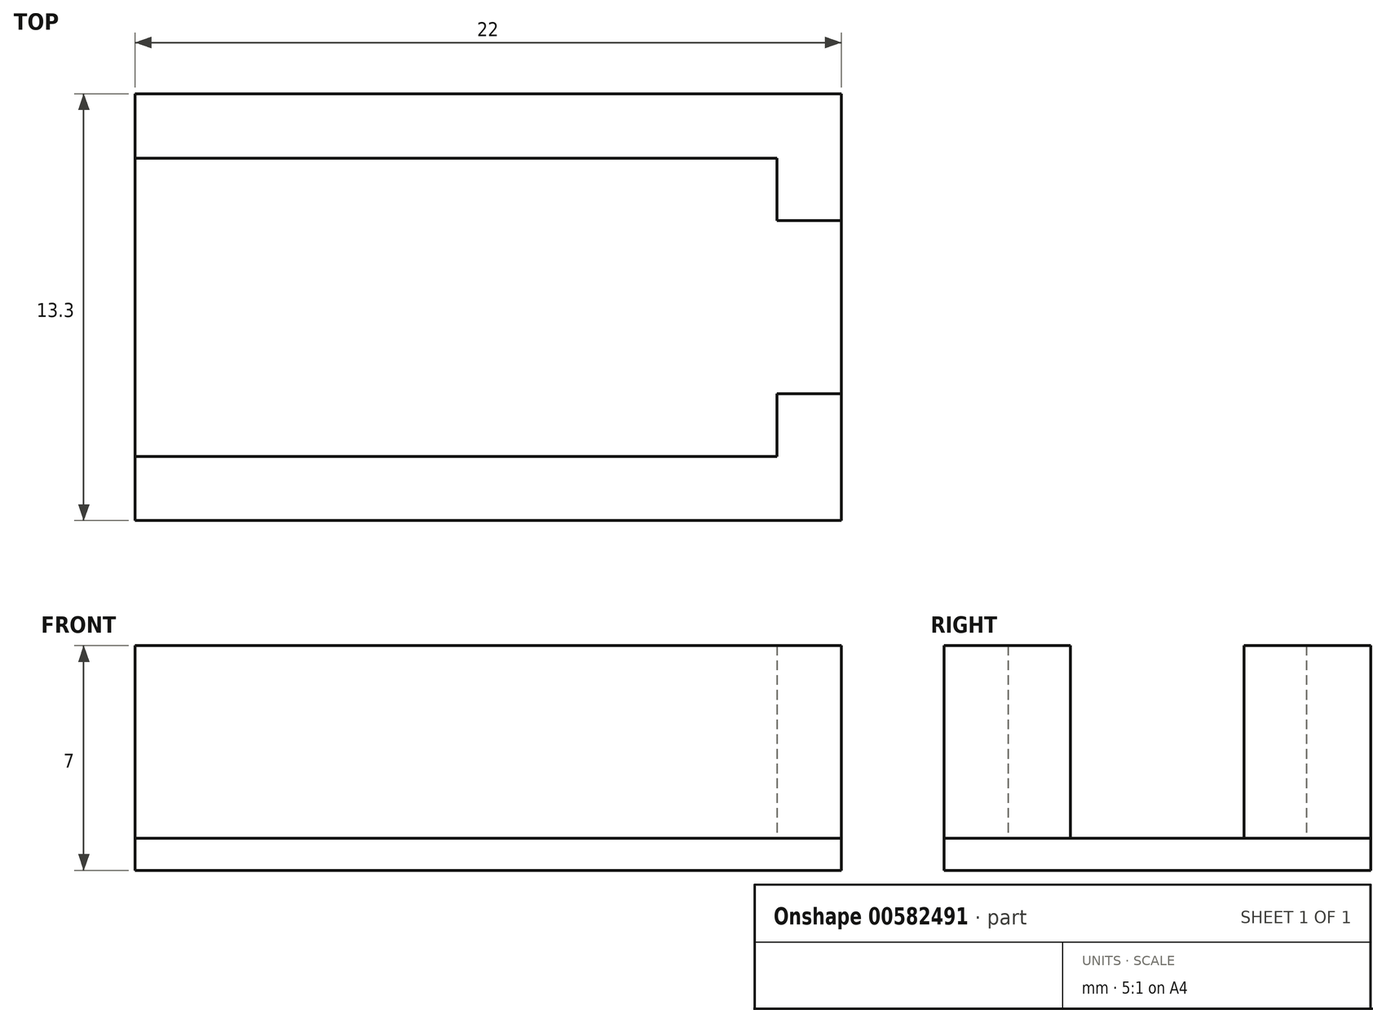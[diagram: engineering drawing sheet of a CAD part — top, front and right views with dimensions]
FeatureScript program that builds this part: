
annotation { "Feature Type Name" : "Feature", "Feature Type Description" : "" }
export const myFeature = defineFeature(function(context is Context, id is Id, definition is map)
    precondition{}
    {
        {
            var Q0;
            Q0=qCreatedBy(makeId("Top.planeOp"),FACE);
            var sketch = newSketch(context, id + "F0", { "sketchPlane" : qUnion([Q0])});
            skLineSegment(sketch, "E0.bottom", {"start": v(5, 4.65) * mm, "end": v(-5, 4.65) * mm});
            skLineSegment(sketch, "E0.top", {"start": v(5, -4.65) * mm, "end": v(-5, -4.65) * mm});
            skLineSegment(sketch, "E0.left", {"start": v(5, 4.65) * mm, "end": v(5, -4.65) * mm});
            skLineSegment(sketch, "E0.right", {"start": v(-5, 4.65) * mm, "end": v(-5, -4.65) * mm});
            skPoint(sketch, "E0.middle", {"position": v(0, 0) * mm});
            skLineSegment(sketch, "E1.0", {"start": v(5, 6.65) * mm, "end": v(-5, 6.65) * mm});
            skLineSegment(sketch, "E2.0", {"start": v(7, 4.85) * mm, "end": v(7, -4.85) * mm});
            skLineSegment(sketch, "E3.0", {"start": v(5, -6.65) * mm, "end": v(-5, -6.65) * mm});
            skLineSegment(sketch, "E4", {"start": v(5, -6.65) * mm, "end": v(7, -6.65) * mm});
            skLineSegment(sketch, "E5", {"start": v(7, -6.65) * mm, "end": v(7, -4.85) * mm});
            skLineSegment(sketch, "E6", {"start": v(7, 4.85) * mm, "end": v(7, 6.65) * mm});
            skLineSegment(sketch, "E7", {"start": v(7, 6.65) * mm, "end": v(5, 6.65) * mm});
            skLineSegment(sketch, "E8", {"start": v(-5, 6.65) * mm, "end": v(-5, 4.65) * mm});
            skLineSegment(sketch, "E9", {"start": v(-5, -6.65) * mm, "end": v(-5, -4.65) * mm});
            skLineSegment(sketch, "E10", {"start": v(5, 0) * mm, "end": v(7, 0) * mm});
            skLineSegment(sketch, "E11.bottom", {"start": v(7, 2.7) * mm, "end": v(5, 2.7) * mm});
            skLineSegment(sketch, "E11.top", {"start": v(7, -2.7) * mm, "end": v(5, -2.7) * mm});
            skLineSegment(sketch, "E11.left", {"start": v(7, 2.7) * mm, "end": v(7, -2.7) * mm});
            skLineSegment(sketch, "E11.right", {"start": v(5, 2.7) * mm, "end": v(5, -2.7) * mm});
            skPoint(sketch, "E11.middle", {"position": v(6, 0) * mm});
            skLineSegment(sketch, "E12.bottom", {"start": v(-5, 4.65) * mm, "end": v(-15, 4.65) * mm});
            skLineSegment(sketch, "E12.top", {"start": v(-5, 6.65) * mm, "end": v(-15, 6.65) * mm});
            skLineSegment(sketch, "E12.left", {"start": v(-5, 4.65) * mm, "end": v(-5, 6.65) * mm});
            skLineSegment(sketch, "E12.right", {"start": v(-15, 4.65) * mm, "end": v(-15, 6.65) * mm});
            skLineSegment(sketch, "E13.bottom", {"start": v(-5, -6.65) * mm, "end": v(-15, -6.65) * mm});
            skLineSegment(sketch, "E13.top", {"start": v(-5, -4.65) * mm, "end": v(-15, -4.65) * mm});
            skLineSegment(sketch, "E13.right", {"start": v(-15, -6.65) * mm, "end": v(-15, -4.65) * mm});
            skSolve(sketch);
        }
        {
            var Q0;
            {var subQ4=sQuery(id+"F0.wireOp",EDGE,"E0.bottom");Q0=makeQuery(id+"F0.imprint","IMPRINT",FACE,{"disambiguationData":[TD([[makeQuery(id+"F0.imprint","IMPRINT",EDGE,{"derivedFrom":subQ4}),-1.0]])]});}
            var Q1;
            {var subQ4=sQuery(id+"F0.wireOp",EDGE,"E0.top");Q1=makeQuery(id+"F0.imprint","IMPRINT",FACE,{"disambiguationData":[TD([[makeQuery(id+"F0.imprint","IMPRINT",EDGE,{"derivedFrom":subQ4}),1.0]])]});}
            var Q2;
            Q2=makeQuery(id+"F0.imprint","IMPRINT",FACE,{"disambiguationData":[TD([[makeQuery(id+"F0.imprint","IMPRINT",EDGE,{"derivedFrom":sQuery(id+"F0.wireOp",EDGE,"E13.bottom")}),-1.0]])]});
            var Q3;
            Q3=makeQuery(id+"F0.imprint","IMPRINT",FACE,{"disambiguationData":[TD([[makeQuery(id+"F0.imprint","IMPRINT",EDGE,{"derivedFrom":sQuery(id+"F0.wireOp",EDGE,"E12.bottom")}),-1.0]])]});
            extrude(context, id + "F1", {"entities" : qUnion([Q0, Q1, Q2, Q3]), "depth" : 6 * mm, "offsetDistance" : 25 * mm});
        }
        {
            var Q0;
            Q0=qCreatedBy(makeId("Top.planeOp"),FACE);
            var sketch = newSketch(context, id + "F2", { "sketchPlane" : qUnion([Q0])});
            skPoint(sketch, "E14.0", {"position": v(-15, -6.65) * mm});
            skPoint(sketch, "E15.0", {"position": v(7, 6.65) * mm});
            skLineSegment(sketch, "E16.bottom", {"start": v(-15, -6.65) * mm, "end": v(7, -6.65) * mm});
            skLineSegment(sketch, "E16.top", {"start": v(-15, 6.65) * mm, "end": v(7, 6.65) * mm});
            skLineSegment(sketch, "E16.left", {"start": v(-15, -6.65) * mm, "end": v(-15, 6.65) * mm});
            skLineSegment(sketch, "E16.right", {"start": v(7, -6.65) * mm, "end": v(7, 6.65) * mm});
            skSolve(sketch);
        }
        {
            var Q0;
            Q0=makeQuery(id+"F2.imprint","IMPRINT",FACE,{"disambiguationData":[TD([[makeQuery(id+"F2.imprint","IMPRINT",EDGE,{"derivedFrom":sQuery(id+"F2.wireOp",EDGE,"E16.bottom")}),1.0]])]});
            extrude(context, id + "F3", {"entities" : qUnion([Q0]), "oppositeDirection" : true, "depth" : 1 * mm, "offsetDistance" : 25 * mm});
        }
    });
